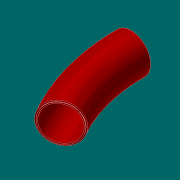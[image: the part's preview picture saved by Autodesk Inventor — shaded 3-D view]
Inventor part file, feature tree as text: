
AUTODESK INVENTOR PART (.ipt)
format: ipt  version: 2017.3 (Build 213257000, 257)  size: 229,888 bytes
history: native  units: in
note: dims shown in document units (in); Inventor stores cm internally (conversion verified against a paired STEP export)
features: extrude x3, sketch x3, revolve x2, fillet x1, chamfer x1
ambient origin geometry x8: Origin, YZ Plane, XZ Plane, XY Plane, X Axis, Y Axis, Z Axis, Center Point
bodies: Solid1 (feature_tree)
feature tree (10):
  revolve  "Revolution1"  [1 undecoded]
  extrude  "Extrusion9"  TaperAngle=30.0deg  [1 undecoded]
  sketch  "Sketch11"  dims[d34=30.5in d35=0.5in d36=0.0in d37=30.48in d38=33.5in d39=0.25in d40=0.0in d41=0.25in d42=0.0in d43=0.0034in d44=0.0312in d45=0.0312in d46=0.125in d47=45.0deg]
  extrude  "Extrusion10"  Depth=0.5in TaperAngle=0.0deg
  extrude  "Extrusion11"  Depth=0.0312in
  revolve  "Revolution2"  [1 undecoded]
  fillet  "Fillet3"  Radius=0.25in
  chamfer  "Chamfer3"  Distance=0.25in
  sketch  "Sketch1"  dims[d0=28.5in d1=32.5in]
  sketch  "Sketch10"  dims[d2=160.0in d3=30.0deg]
note: 3 required parameter values undecoded (feature->parameter linkage not recoverable at this tier; creation-order binding heuristic only, values carry confidence <= 0.55)